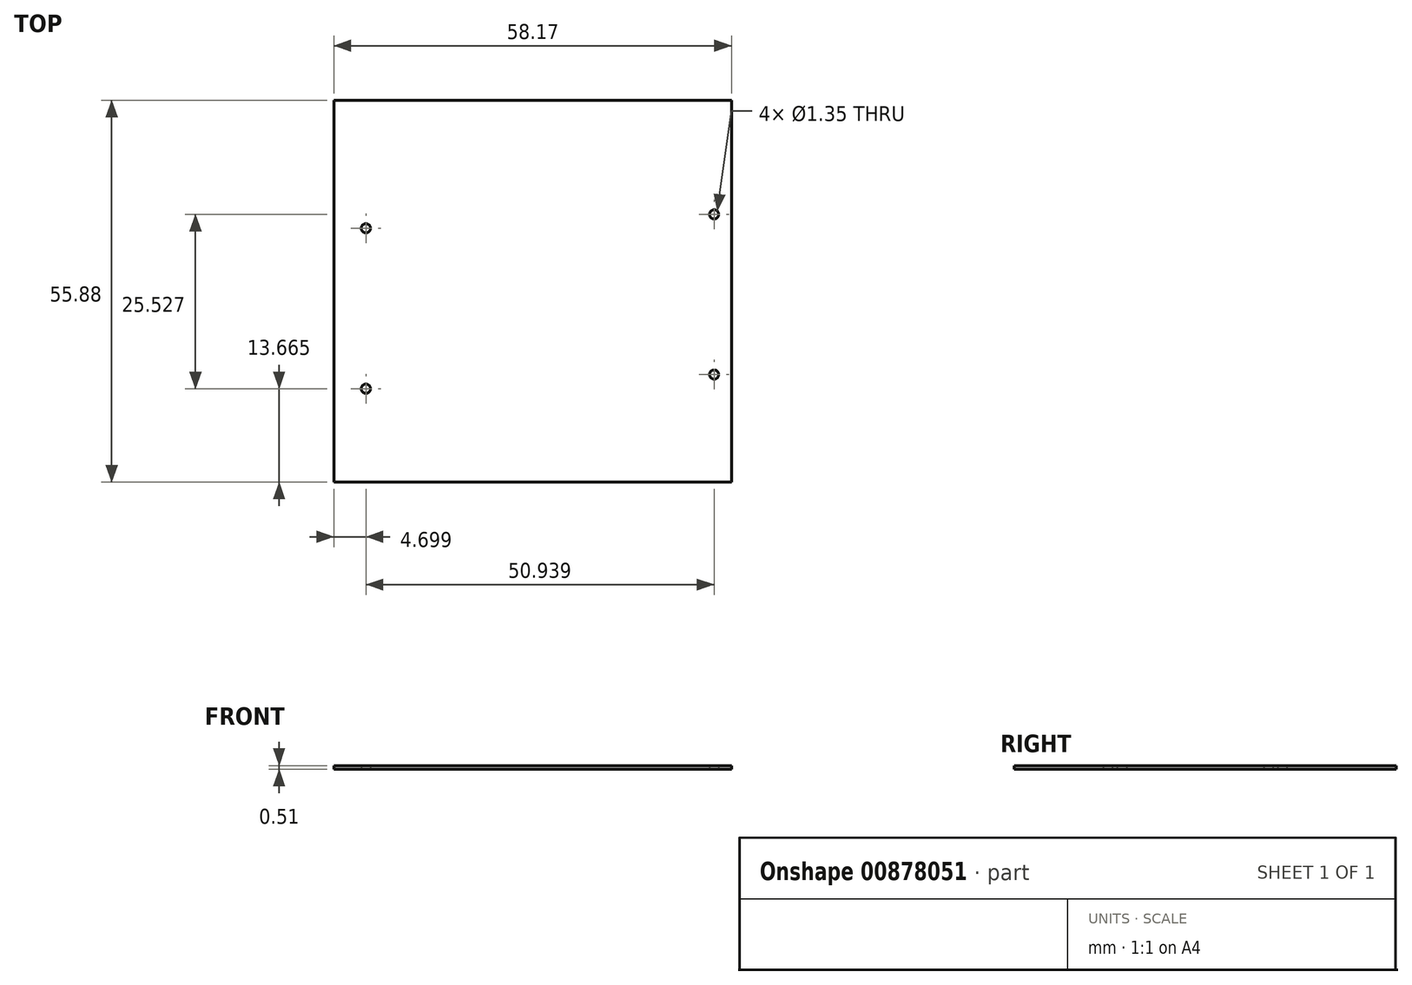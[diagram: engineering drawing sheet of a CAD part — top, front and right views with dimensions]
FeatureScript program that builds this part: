
annotation { "Feature Type Name" : "Feature", "Feature Type Description" : "" }
export const myFeature = defineFeature(function(context is Context, id is Id, definition is map)
    precondition{}
    {
        {
            var Q0;
            Q0=qCreatedBy(makeId("Top.planeOp"),FACE);
            var sketch = newSketch(context, id + "F0", { "sketchPlane" : qUnion([Q0])});
            skLineSegment(sketch, "E0.bottom", {"start": v(0, 0) * mm, "end": v(58.17, 0) * mm});
            skLineSegment(sketch, "E0.top", {"start": v(0, 55.88) * mm, "end": v(58.17, 55.88) * mm});
            skLineSegment(sketch, "E0.left", {"start": v(0, 0) * mm, "end": v(0, 55.88) * mm});
            skLineSegment(sketch, "E0.right", {"start": v(58.17, 0) * mm, "end": v(58.17, 55.88) * mm});
            skLineSegment(sketch, "E1", {"start": v(0, 0) * mm, "end": v(4.7, 0) * mm});
            skLineSegment(sketch, "E2", {"start": v(4.7, 0) * mm, "end": v(4.7, 13.67) * mm});
            skCircle(sketch, "E3", {"center": v(4.7, 13.67) * mm, "radius": 0.67 * mm});
            skLineSegment(sketch, "E4", {"start": v(4.7, 13.67) * mm, "end": v(4.7, 37.16) * mm});
            skCircle(sketch, "E5", {"center": v(4.7, 37.16) * mm, "radius": 0.67 * mm});
            skLineSegment(sketch, "E6", {"start": v(58.17, 0) * mm, "end": v(55.64, 0) * mm});
            skLineSegment(sketch, "E7", {"start": v(55.64, 0) * mm, "end": v(55.64, 15.75) * mm});
            skLineSegment(sketch, "E8", {"start": v(55.64, 15.75) * mm, "end": v(55.64, 39.2) * mm});
            skCircle(sketch, "E9", {"center": v(55.64, 39.2) * mm, "radius": 0.67 * mm});
            skCircle(sketch, "E10", {"center": v(55.64, 15.75) * mm, "radius": 0.67 * mm});
            skSolve(sketch);
        }
        {
            var Q0;
            Q0=makeQuery(id+"F0.imprint","IMPRINT",FACE,{"disambiguationData":[TD([[makeQuery(id+"F0.imprint","IMPRINT",EDGE,{"derivedFrom":sQuery(id+"F0.wireOp",EDGE,"E0.bottom")}),1.0]])]});
            extrude(context, id + "F1", {"entities" : qUnion([Q0]), "depth" : 0.5 * mm, "offsetDistance" : 25.4 * mm});
        }
    });
